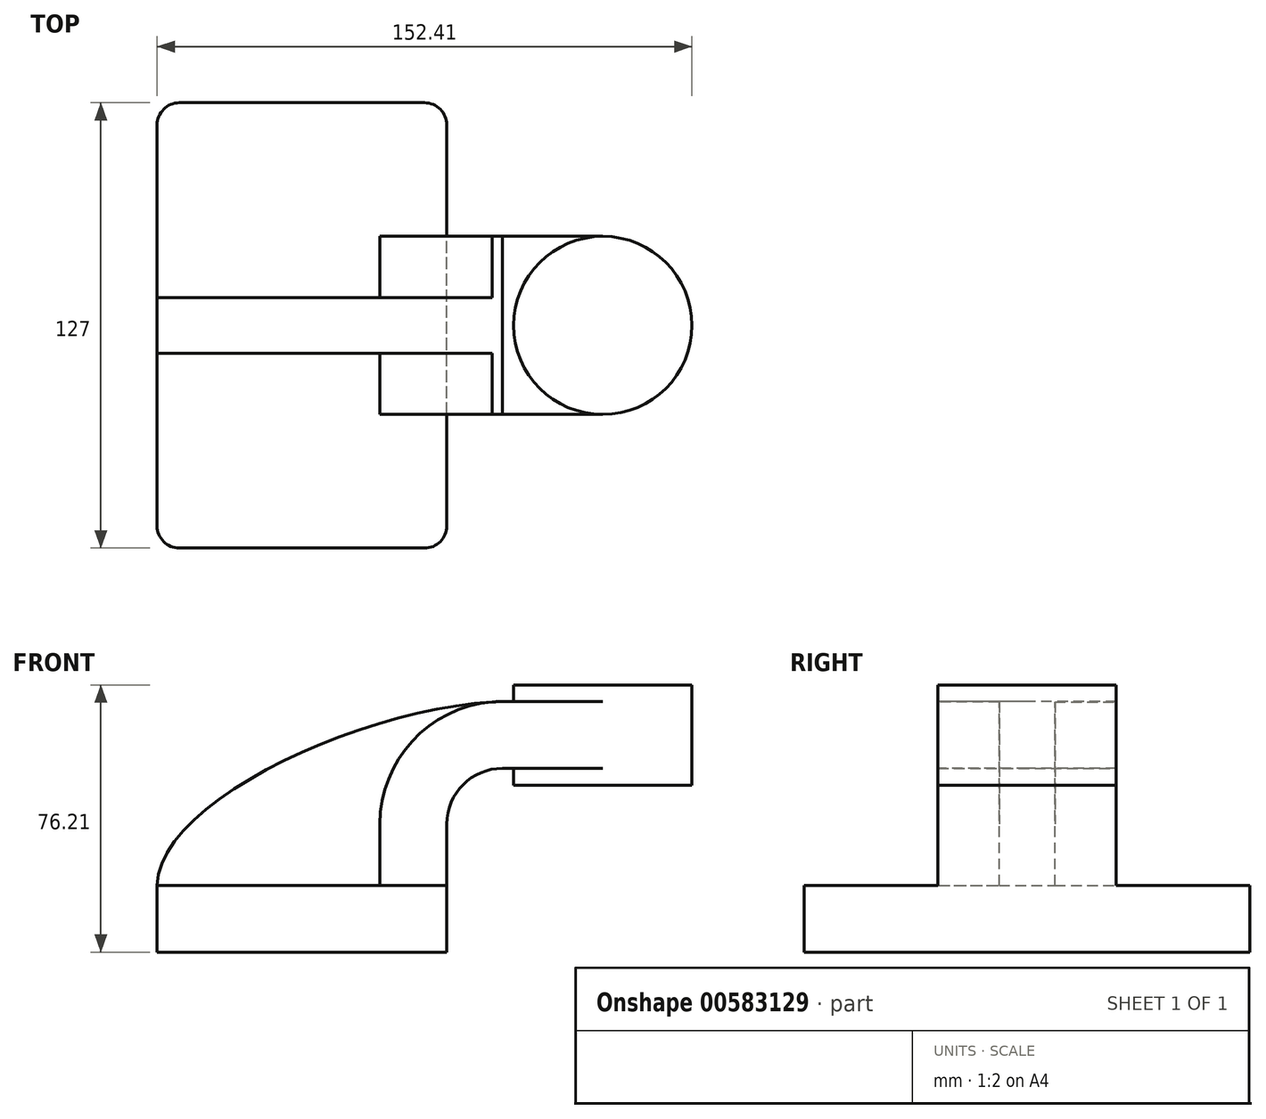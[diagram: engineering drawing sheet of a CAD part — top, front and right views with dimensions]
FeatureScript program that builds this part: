
annotation { "Feature Type Name" : "Feature", "Feature Type Description" : "" }
export const myFeature = defineFeature(function(context is Context, id is Id, definition is map)
    precondition{}
    {
        {
            var Q0;
            Q0=qCreatedBy(makeId("Front.planeOp"),FACE);
            var sketch = newSketch(context, id + "F0", { "sketchPlane" : qUnion([Q0])});
            skLineSegment(sketch, "E0.bottom", {"start": v(41.27, 9.53) * mm, "end": v(-41.28, 9.53) * mm});
            skLineSegment(sketch, "E0.top", {"start": v(41.28, -9.52) * mm, "end": v(-41.27, -9.52) * mm});
            skLineSegment(sketch, "E0.left", {"start": v(41.28, 9.53) * mm, "end": v(41.28, -9.52) * mm});
            skLineSegment(sketch, "E0.right", {"start": v(-41.28, 9.53) * mm, "end": v(-41.27, -9.52) * mm});
            skPoint(sketch, "E0.middle", {"position": v(0, 0) * mm});
            skLineSegment(sketch, "E1.bottom", {"start": v(111.13, 38.1) * mm, "end": v(60.33, 38.1) * mm});
            skLineSegment(sketch, "E1.top", {"start": v(111.13, 66.68) * mm, "end": v(60.33, 66.68) * mm});
            skLineSegment(sketch, "E1.left", {"start": v(111.13, 38.1) * mm, "end": v(111.13, 66.68) * mm});
            skLineSegment(sketch, "E1.right", {"start": v(60.33, 38.1) * mm, "end": v(60.33, 66.67) * mm});
            skPoint(sketch, "E1.middle", {"position": v(85.73, 52.39) * mm});
            skLineSegment(sketch, "E2", {"start": v(41.27, 9.53) * mm, "end": v(41.27, 27) * mm});
            skArc(sketch, "E3", {"start": v(41.28, 27) * mm, "mid": v(45.92, 38.23) * mm, "end": v(57.15, 42.88) * mm});
            skLineSegment(sketch, "E4", {"start": v(57.15, 42.88) * mm, "end": v(85.73, 42.88) * mm});
            skPoint(sketch, "E4.endSnap0", {"position": v(85.73, 38.1) * mm});
            skLineSegment(sketch, "E5.0", {"start": v(57.15, 61.93) * mm, "end": v(85.73, 61.93) * mm});
            skArc(sketch, "E5.1", {"start": v(22.23, 27) * mm, "mid": v(32.45, 51.7) * mm, "end": v(57.15, 61.93) * mm});
            skLineSegment(sketch, "E5.2", {"start": v(22.23, 9.53) * mm, "end": v(22.23, 27) * mm});
            skLineSegment(sketch, "E6", {"start": v(85.73, 38.1) * mm, "end": v(85.73, 66.68) * mm});
            skFitSpline(sketch, "E7", {"points": [v(-41.28, 9.53) * mm, v(57.15, 61.93) * mm], "startDerivative": vector(0.83, 73.07) * mm, "endDerivative": vector(113.91, 2.92) * mm});
            skSolve(sketch);
        }
        {
            var Q0;
            Q0=makeQuery(id+"F0.imprint","IMPRINT",FACE,{"disambiguationData":[TD([[makeQuery(id+"F0.imprint","IMPRINT",EDGE,{"derivedFrom":sQuery(id+"F0.wireOp",EDGE,"E0.top")}),-1.0]])]});
            extrude(context, id + "F1", {"entities" : qUnion([Q0]), "endBound" : BoundingType.SYMMETRIC, "depth" : 127 * mm, "offsetDistance" : 25.4 * mm});
        }
        {
            var Q0;
            {var subQ1=sQuery(id+"F0.wireOp",EDGE,"E2");Q0=makeQuery(id+"F0.imprint","IMPRINT",FACE,{"disambiguationData":[TD([[makeQuery(id+"F0.imprint","IMPRINT",EDGE,{"derivedFrom":subQ1}),1.0]])]});}
            var Q1;
            {var subQ0=sQuery(id+"F0.wireOp",EDGE,"E4");var subQ1=sQuery(id+"F0.wireOp",EDGE,"E1.right");var subQ2=makeQuery(id+"F0.imprint","INTERSECT",VERTEX,{"derivedFrom":[subQ1,subQ0]});Q1=makeQuery(id+"F0.imprint","IMPRINT",FACE,{"disambiguationData":[TD([[makeQuery(id+"F0.imprint","IMPRINT",EDGE,{"disambiguationData":[TD([[subQ2,-1.0]])],"derivedFrom":subQ1}),-1.0]])]});}
            extrude(context, id + "F2", {"entities" : qUnion([Q0, Q1]), "operationType" : NewBodyOperationType.ADD, "endBound" : BoundingType.SYMMETRIC, "depth" : 50.8 * mm, "offsetDistance" : 25.4 * mm});
        }
        {
            var Q0;
            {var subQ3=sQuery(id+"F0.wireOp",EDGE,"E5.2");Q0=makeQuery(id+"F0.imprint","IMPRINT",FACE,{"disambiguationData":[TD([[makeQuery(id+"F0.imprint","IMPRINT",EDGE,{"derivedFrom":subQ3}),1.0]])]});}
            extrude(context, id + "F3", {"entities" : qUnion([Q0]), "operationType" : NewBodyOperationType.ADD, "endBound" : BoundingType.SYMMETRIC, "depth" : 15.88 * mm, "offsetDistance" : 25.4 * mm});
        }
        {
            var Q0;
            {var subQ0=sQuery(id+"F0.wireOp",EDGE,"E1.left");Q0=makeQuery(id+"F0.imprint","IMPRINT",FACE,{"disambiguationData":[TD([[makeQuery(id+"F0.imprint","IMPRINT",EDGE,{"derivedFrom":subQ0}),1.0]])]});}
            var Q1;
            Q1=sQuery(id+"F0.wireOp",EDGE,"E6");
            revolve(context, id + "F4", {"operationType" : NewBodyOperationType.ADD, "entities" : qUnion([Q0]), "axis" : qUnion([Q1]), "revolveType" : RevolveType.FULL});
        }
        {
            var Q0;
            Q0=makeQuery(id+"F1.opExtrude","CAP_EDGE",EDGE,{"disambiguationData":[OSD([sQuery(id+"F0.wireOp",EDGE,"E0.left")])],"isStart":false});
            var Q1;
            Q1=makeQuery(id+"F1.opExtrude","CAP_EDGE",EDGE,{"disambiguationData":[OSD([sQuery(id+"F0.wireOp",EDGE,"E0.right")])],"isStart":false});
            var Q2;
            Q2=makeQuery(id+"F1.opExtrude","CAP_EDGE",EDGE,{"disambiguationData":[OSD([sQuery(id+"F0.wireOp",EDGE,"E0.left")])],"isStart":true});
            var Q3;
            Q3=makeQuery(id+"F1.opExtrude","CAP_EDGE",EDGE,{"disambiguationData":[OSD([sQuery(id+"F0.wireOp",EDGE,"E0.right")])],"isStart":true});
            fillet(context, id + "F5", {"entities" : qUnion([Q0, Q1, Q2, Q3]), "radius" : 6.35 * mm, "tangentPropagation" : true, "allowEdgeOverflow" : false});
        }
    });
